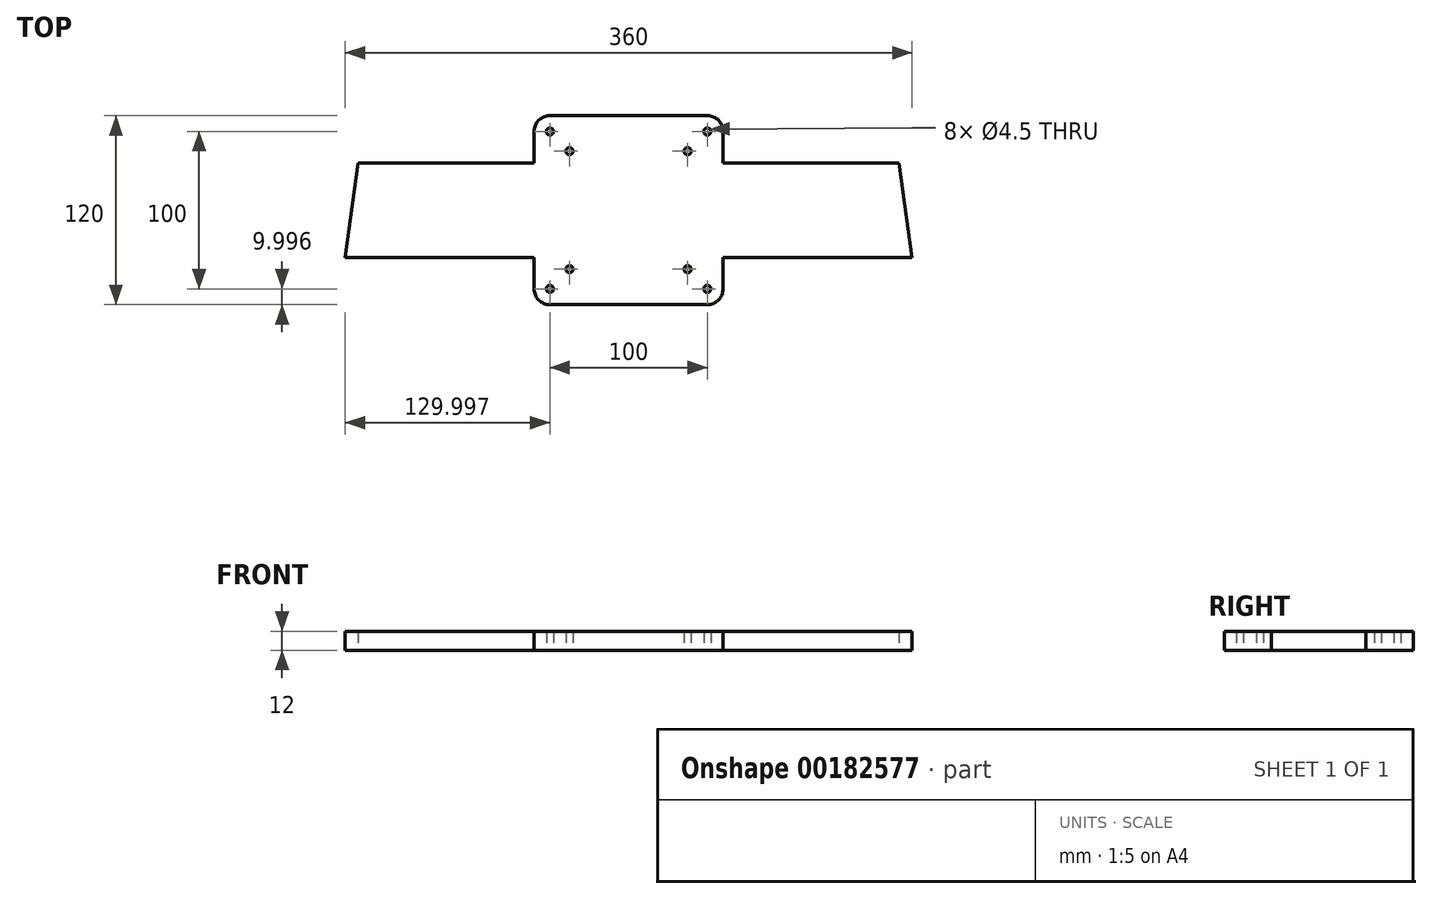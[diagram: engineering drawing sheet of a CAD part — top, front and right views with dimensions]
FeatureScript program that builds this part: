
annotation { "Feature Type Name" : "Feature", "Feature Type Description" : "" }
export const myFeature = defineFeature(function(context is Context, id is Id, definition is map)
    precondition{}
    {
        {
            var Q0;
            Q0=qCreatedBy(makeId("Top.planeOp"),FACE);
            var sketch = newSketch(context, id + "F0", { "sketchPlane" : qUnion([Q0])});
            skLineSegment(sketch, "E0.bottom", {"start": v(7.62, -0.14) * mm, "end": v(107.62, -0.14) * mm});
            skLineSegment(sketch, "E0.top", {"start": v(7.62, 119.86) * mm, "end": v(107.62, 119.86) * mm});
            skLineSegment(sketch, "E0.left", {"start": v(-2.38, 9.86) * mm, "end": v(-2.38, 29.86) * mm});
            skLineSegment(sketch, "E0.right", {"start": v(117.62, 9.86) * mm, "end": v(117.62, 29.86) * mm});
            skArc(sketch, "E1", {"start": v(117.62, 109.86) * mm, "mid": v(114.69, 116.93) * mm, "end": v(107.62, 119.86) * mm});
            skArc(sketch, "E2", {"start": v(107.62, -0.14) * mm, "mid": v(114.69, 2.78) * mm, "end": v(117.62, 9.86) * mm});
            skArc(sketch, "E3", {"start": v(-2.38, 9.86) * mm, "mid": v(0.55, 2.78) * mm, "end": v(7.62, -0.14) * mm});
            skArc(sketch, "E4", {"start": v(7.62, 119.86) * mm, "mid": v(0.55, 116.93) * mm, "end": v(-2.38, 109.86) * mm});
            skCircle(sketch, "E5", {"center": v(57.62, 59.86) * mm, "radius": 60 * mm, "construction": true});
            skLineSegment(sketch, "E6.bottom", {"start": v(107.62, 109.86) * mm, "end": v(7.62, 109.86) * mm, "construction": true});
            skLineSegment(sketch, "E6.top", {"start": v(107.62, 9.86) * mm, "end": v(7.62, 9.86) * mm, "construction": true});
            skLineSegment(sketch, "E6.left", {"start": v(107.62, 109.86) * mm, "end": v(107.62, 9.86) * mm, "construction": true});
            skLineSegment(sketch, "E6.right", {"start": v(7.62, 109.86) * mm, "end": v(7.62, 9.86) * mm, "construction": true});
            skLineSegment(sketch, "E7.bottom", {"start": v(95.12, 97.36) * mm, "end": v(20.12, 97.36) * mm, "construction": true});
            skLineSegment(sketch, "E7.top", {"start": v(95.12, 22.36) * mm, "end": v(20.12, 22.36) * mm, "construction": true});
            skLineSegment(sketch, "E7.left", {"start": v(95.12, 97.36) * mm, "end": v(95.12, 22.36) * mm, "construction": true});
            skLineSegment(sketch, "E7.right", {"start": v(20.12, 97.36) * mm, "end": v(20.12, 22.36) * mm, "construction": true});
            skCircle(sketch, "E8", {"center": v(20.12, 97.36) * mm, "radius": 2.25 * mm});
            skCircle(sketch, "E9", {"center": v(7.62, 109.86) * mm, "radius": 2.25 * mm});
            skCircle(sketch, "E10", {"center": v(107.62, 109.86) * mm, "radius": 2.25 * mm});
            skCircle(sketch, "E11", {"center": v(95.12, 97.36) * mm, "radius": 2.25 * mm});
            skCircle(sketch, "E12", {"center": v(95.12, 22.36) * mm, "radius": 2.25 * mm});
            skCircle(sketch, "E13", {"center": v(107.62, 9.86) * mm, "radius": 2.25 * mm});
            skCircle(sketch, "E14", {"center": v(7.62, 9.86) * mm, "radius": 2.25 * mm});
            skCircle(sketch, "E15", {"center": v(20.12, 22.36) * mm, "radius": 2.25 * mm});
            skLineSegment(sketch, "E16.bottom", {"start": v(229.46, 89.86) * mm, "end": v(117.62, 89.86) * mm});
            skLineSegment(sketch, "E16.top", {"start": v(237.62, 29.86) * mm, "end": v(117.62, 29.86) * mm});
            skLineSegment(sketch, "E17", {"start": v(237.62, 29.86) * mm, "end": v(229.46, 89.86) * mm});
            skLineSegment(sketch, "E18", {"start": v(-122.38, 29.86) * mm, "end": v(-114.23, 89.86) * mm});
            skPoint(sketch, "E19.orphan", {"position": v(237.62, 89.86) * mm});
            skPoint(sketch, "E16.right.start.orphan", {"position": v(-122.38, 89.86) * mm});
            skLineSegment(sketch, "E20.trimOffspring", {"start": v(-2.38, 89.86) * mm, "end": v(-114.23, 89.86) * mm});
            skLineSegment(sketch, "E21.trimOffspring", {"start": v(117.62, 89.86) * mm, "end": v(117.62, 109.86) * mm});
            skLineSegment(sketch, "E22.trimOffspring", {"start": v(-2.38, 29.86) * mm, "end": v(-122.38, 29.86) * mm});
            skLineSegment(sketch, "E23.trimOffspring", {"start": v(-2.38, 89.86) * mm, "end": v(-2.38, 109.86) * mm});
            skLineSegment(sketch, "E24", {"start": v(-2.38, 89.86) * mm, "end": v(-2.38, 29.86) * mm, "construction": true});
            skLineSegment(sketch, "E25", {"start": v(117.62, 89.86) * mm, "end": v(117.62, 29.86) * mm, "construction": true});
            skSolve(sketch);
        }
        {
            var Q0;
            Q0 = qSketchRegion(id + "F0", true);
            extrude(context, id + "F1", {"entities" : qUnion([Q0]), "depth" : 12 * mm});
        }
    });
